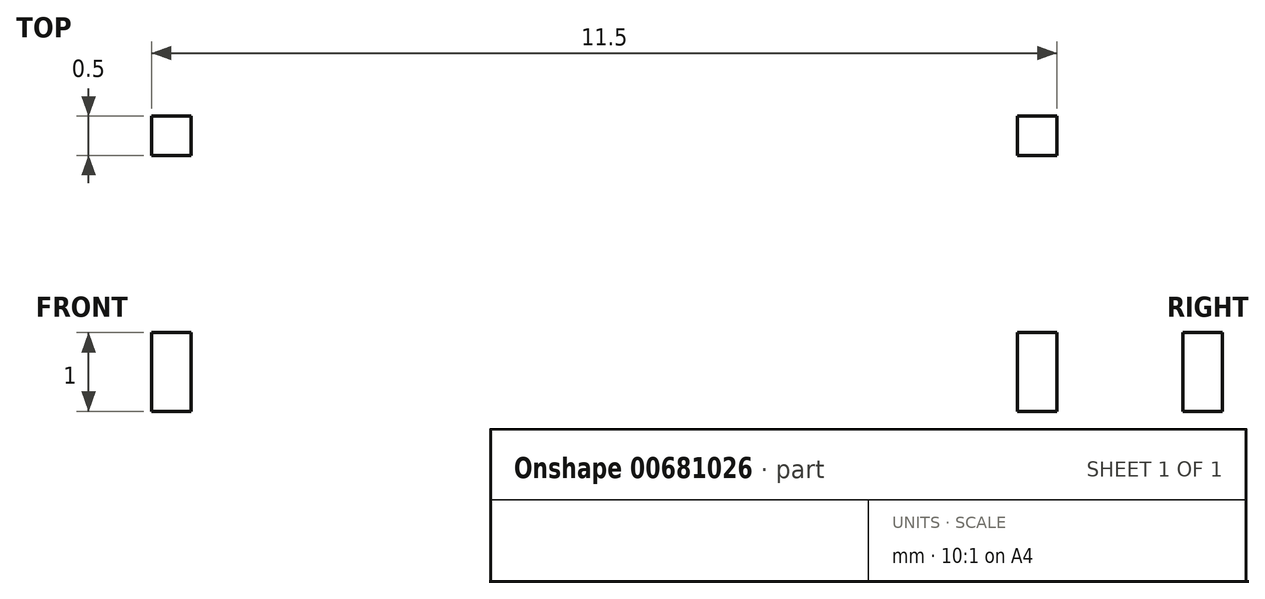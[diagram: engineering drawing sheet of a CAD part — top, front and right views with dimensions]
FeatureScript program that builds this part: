
annotation { "Feature Type Name" : "Feature", "Feature Type Description" : "" }
export const myFeature = defineFeature(function(context is Context, id is Id, definition is map)
    precondition{}
    {
        {
            var Q0;
            Q0=qCreatedBy(makeId("Top.planeOp"),FACE);
            var sketch = newSketch(context, id + "F0", { "sketchPlane" : qUnion([Q0])});
            skLineSegment(sketch, "E0.bottom", {"start": v(5.75, -5.5) * mm, "end": v(-5.75, -5.5) * mm});
            skLineSegment(sketch, "E0.top", {"start": v(5.75, 5.5) * mm, "end": v(-5.75, 5.5) * mm});
            skLineSegment(sketch, "E0.left", {"start": v(5.75, -5.5) * mm, "end": v(5.75, 5.5) * mm});
            skLineSegment(sketch, "E0.right", {"start": v(-5.75, -5.5) * mm, "end": v(-5.75, 5.5) * mm});
            skPoint(sketch, "E0.middle", {"position": v(0, 0) * mm});
            skLineSegment(sketch, "E1.bottom", {"start": v(-5.75, 5.5) * mm, "end": v(-5.25, 5.5) * mm});
            skLineSegment(sketch, "E1.top", {"start": v(-5.75, 5) * mm, "end": v(-5.25, 5) * mm});
            skLineSegment(sketch, "E1.left", {"start": v(-5.75, 5.5) * mm, "end": v(-5.75, 5) * mm});
            skLineSegment(sketch, "E1.right", {"start": v(-5.25, 5.5) * mm, "end": v(-5.25, 5) * mm});
            skLineSegment(sketch, "E2.bottom", {"start": v(-5.75, 5) * mm, "end": v(-4.75, 5) * mm});
            skLineSegment(sketch, "E2.top", {"start": v(-5.75, 4.5) * mm, "end": v(-4.75, 4.5) * mm});
            skLineSegment(sketch, "E2.left", {"start": v(-5.75, 5) * mm, "end": v(-5.75, 4.5) * mm});
            skLineSegment(sketch, "E2.right", {"start": v(-4.75, 5) * mm, "end": v(-4.75, 4.5) * mm});
            skLineSegment(sketch, "E3.bottom", {"start": v(5.75, 5.5) * mm, "end": v(5.25, 5.5) * mm});
            skLineSegment(sketch, "E3.top", {"start": v(5.75, 5) * mm, "end": v(5.25, 5) * mm});
            skLineSegment(sketch, "E3.left", {"start": v(5.75, 5.5) * mm, "end": v(5.75, 5) * mm});
            skLineSegment(sketch, "E3.right", {"start": v(5.25, 5.5) * mm, "end": v(5.25, 5) * mm});
            skLineSegment(sketch, "E4.bottom", {"start": v(5.75, 5) * mm, "end": v(4.75, 5) * mm});
            skLineSegment(sketch, "E4.top", {"start": v(5.75, 4.5) * mm, "end": v(4.75, 4.5) * mm});
            skLineSegment(sketch, "E4.left", {"start": v(5.75, 5) * mm, "end": v(5.75, 4.5) * mm});
            skLineSegment(sketch, "E4.right", {"start": v(4.75, 5) * mm, "end": v(4.75, 4.5) * mm});
            skLineSegment(sketch, "E5.bottom", {"start": v(-5.75, -5.5) * mm, "end": v(-5.25, -5.5) * mm});
            skLineSegment(sketch, "E5.top", {"start": v(-5.75, -5) * mm, "end": v(-5.25, -5) * mm});
            skLineSegment(sketch, "E5.left", {"start": v(-5.75, -5.5) * mm, "end": v(-5.75, -5) * mm});
            skLineSegment(sketch, "E5.right", {"start": v(-5.25, -5.5) * mm, "end": v(-5.25, -5) * mm});
            skLineSegment(sketch, "E6.bottom", {"start": v(5.75, -5.5) * mm, "end": v(5.25, -5.5) * mm});
            skLineSegment(sketch, "E6.top", {"start": v(5.75, -5) * mm, "end": v(5.25, -5) * mm});
            skLineSegment(sketch, "E6.left", {"start": v(5.75, -5.5) * mm, "end": v(5.75, -5) * mm});
            skLineSegment(sketch, "E6.right", {"start": v(5.25, -5.5) * mm, "end": v(5.25, -5) * mm});
            skLineSegment(sketch, "E7.bottom", {"start": v(-5.25, -5) * mm, "end": v(5.25, -5) * mm});
            skLineSegment(sketch, "E7.top", {"start": v(-5.25, -4.5) * mm, "end": v(5.25, -4.5) * mm});
            skLineSegment(sketch, "E7.left", {"start": v(-5.25, -5) * mm, "end": v(-5.25, -4.5) * mm});
            skLineSegment(sketch, "E7.right", {"start": v(5.25, -5) * mm, "end": v(5.25, -4.5) * mm});
            skLineSegment(sketch, "E8.bottom", {"start": v(-5.25, -5.5) * mm, "end": v(-4.75, -5.5) * mm});
            skLineSegment(sketch, "E8.top", {"start": v(-5.25, -5) * mm, "end": v(-4.75, -5) * mm});
            skLineSegment(sketch, "E8.right", {"start": v(-4.75, -5.5) * mm, "end": v(-4.75, -5) * mm});
            skLineSegment(sketch, "E9.bottom", {"start": v(5.25, -5.5) * mm, "end": v(4.75, -5.5) * mm});
            skLineSegment(sketch, "E9.top", {"start": v(5.25, -5) * mm, "end": v(4.75, -5) * mm});
            skLineSegment(sketch, "E9.right", {"start": v(4.75, -5.5) * mm, "end": v(4.75, -5) * mm});
            skLineSegment(sketch, "E10.bottom", {"start": v(-4.75, -5.5) * mm, "end": v(4.75, -5.5) * mm});
            skLineSegment(sketch, "E10.top", {"start": v(-4.75, -5) * mm, "end": v(4.75, -5) * mm});
            skSolve(sketch);
        }
        {
            var Q0;
            Q0=makeQuery(id+"F0.imprint","IMPRINT",FACE,{"disambiguationData":[TD([[makeQuery(id+"F0.imprint","IMPRINT",EDGE,{"derivedFrom":sQuery(id+"F0.wireOp",EDGE,"E0.top")}),1.0]])]});
            var Q1;
            Q1=makeQuery(id+"F0.imprint","IMPRINT",FACE,{"disambiguationData":[TD([[makeQuery(id+"F0.imprint","IMPRINT",EDGE,{"derivedFrom":sQuery(id+"F0.wireOp",EDGE,"E5.bottom")}),1.0]])]});
            var Q2;
            Q2=makeQuery(id+"F0.imprint","IMPRINT",FACE,{"disambiguationData":[TD([[makeQuery(id+"F0.imprint","IMPRINT",EDGE,{"derivedFrom":sQuery(id+"F0.wireOp",EDGE,"E8.bottom")}),1.0]])]});
            var Q3;
            Q3=makeQuery(id+"F0.imprint","IMPRINT",FACE,{"disambiguationData":[TD([[makeQuery(id+"F0.imprint","IMPRINT",EDGE,{"derivedFrom":sQuery(id+"F0.wireOp",EDGE,"E9.bottom")}),-1.0]])]});
            var Q4;
            Q4=makeQuery(id+"F0.imprint","IMPRINT",FACE,{"disambiguationData":[TD([[makeQuery(id+"F0.imprint","IMPRINT",EDGE,{"derivedFrom":sQuery(id+"F0.wireOp",EDGE,"E6.bottom")}),-1.0]])]});
            extrude(context, id + "F1", {"entities" : qUnion([Q0, Q1, Q2, Q3, Q4]), "depth" : 1 * mm, "offsetDistance" : 25 * mm});
        }
    });
